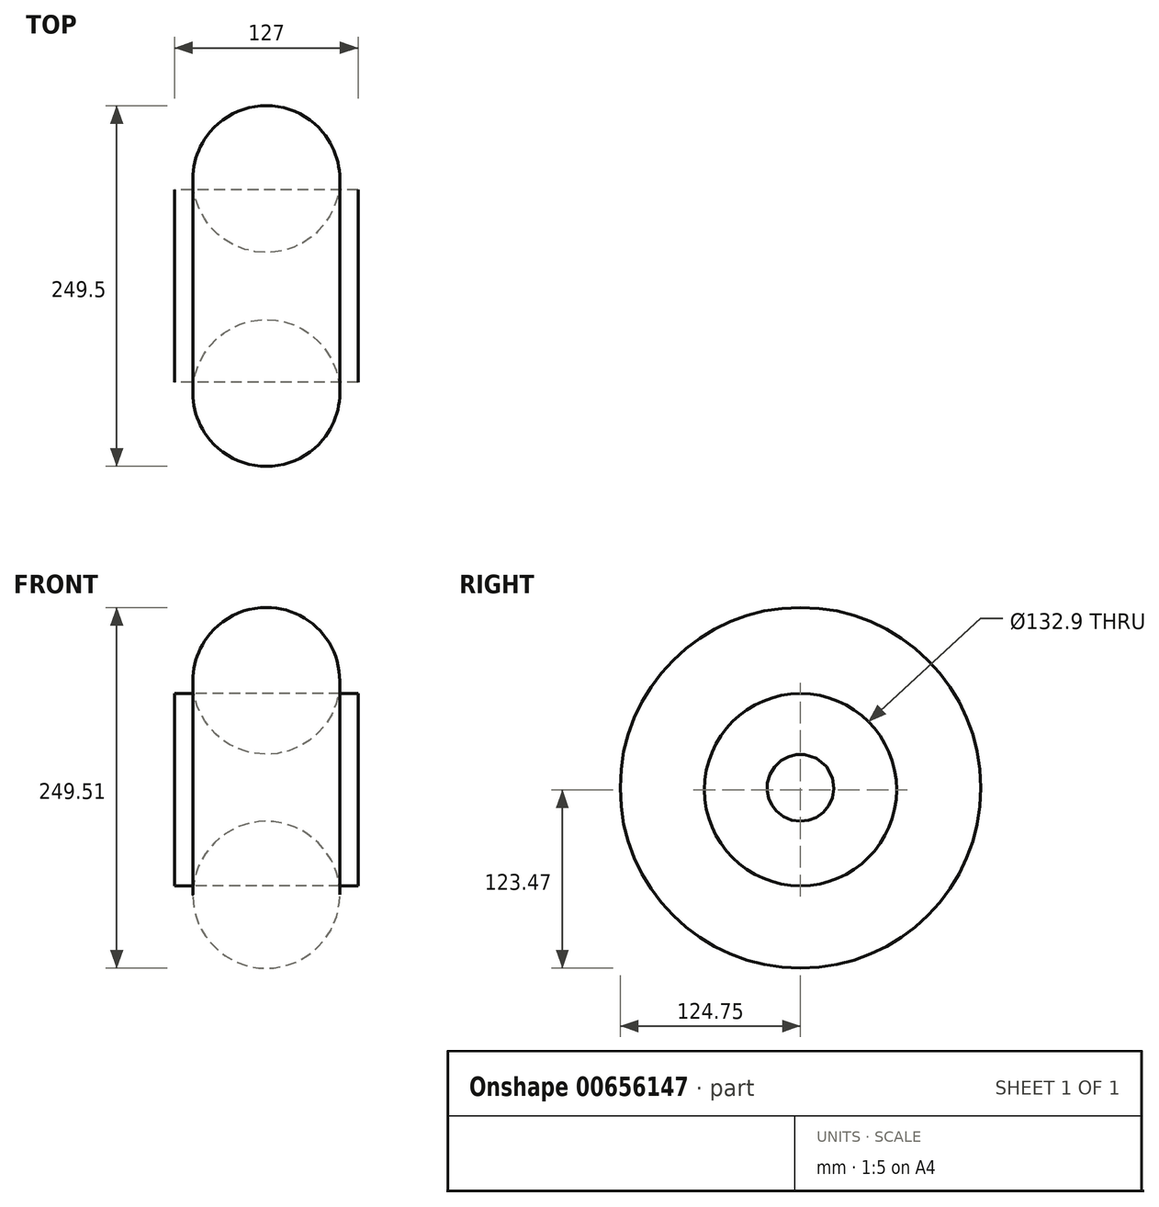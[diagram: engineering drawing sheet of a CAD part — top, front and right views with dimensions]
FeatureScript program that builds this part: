
annotation { "Feature Type Name" : "Feature", "Feature Type Description" : "" }
export const myFeature = defineFeature(function(context is Context, id is Id, definition is map)
    precondition{}
    {
        {
            var Q0;
            Q0=qCreatedBy(makeId("Front.planeOp"),FACE);
            var sketch = newSketch(context, id + "F0", { "sketchPlane" : qUnion([Q0])});
            skCircle(sketch, "E0", {"center": v(0, 0) * mm, "radius": 50.8 * mm});
            skLineSegment(sketch, "E1", {"start": v(-75.2, -73.95) * mm, "end": v(69.25, -73.95) * mm, "construction": true});
            skSolve(sketch);
        }
        {
            var Q0;
            Q0 = qSketchRegion(id + "F0", true);
            var Q1;
            Q1=sQuery(id+"F0.wireOp",EDGE,"E0");
            var Q2;
            Q2=sQuery(id+"F0.wireOp",EDGE,"E1");
            revolve(context, id + "F1", {"bodyType" : ToolBodyType.SURFACE, "entities" : qUnion([Q0]), "surfaceEntities" : qUnion([Q1]), "axis" : qUnion([Q2]), "revolveType" : RevolveType.FULL});
        }
        {
            var Q0;
            Q0=qCreatedBy(makeId("Right.planeOp"),FACE);
            var sketch = newSketch(context, id + "F2", { "sketchPlane" : qUnion([Q0])});
            skCircle(sketch, "E2", {"center": v(0, -75.24) * mm, "radius": 66.45 * mm});
            skSolve(sketch);
        }
        {
            var Q0;
            Q0 = qSketchRegion(id + "F2", true);
            var Q1;
            Q1=sQuery(id+"F2.wireOp",EDGE,"E2");
            extrude(context, id + "F3", {"entities" : qUnion([Q0]), "bodyType" : ToolBodyType.SURFACE, "operationType" : NewBodyOperationType.REMOVE, "surfaceEntities" : qUnion([Q1]), "endBound" : BoundingType.SYMMETRIC, "oppositeDirection" : true, "depth" : 127 * mm, "offsetDistance" : 25.4 * mm});
        }
    });
